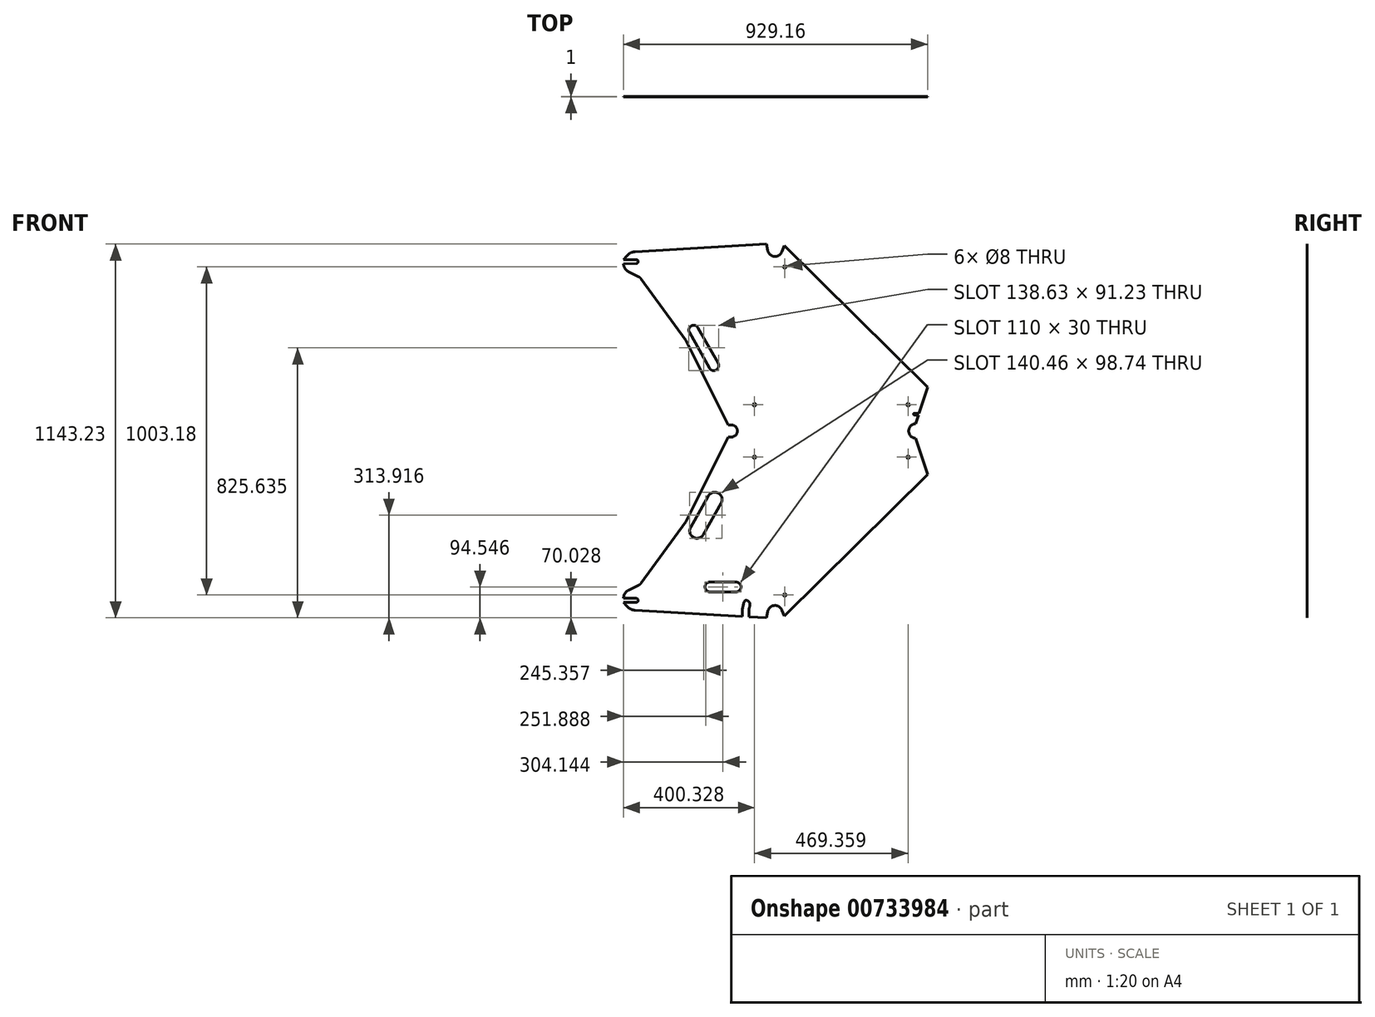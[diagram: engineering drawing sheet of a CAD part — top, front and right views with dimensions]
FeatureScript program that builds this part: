
annotation { "Feature Type Name" : "Feature", "Feature Type Description" : "" }
export const myFeature = defineFeature(function(context is Context, id is Id, definition is map)
    precondition{}
    {
        {
            var Q0;
            Q0=qCreatedBy(makeId("Front.planeOp"),FACE);
            var sketch = newSketch(context, id + "F0", { "sketchPlane" : qUnion([Q0])});
            skLineSegment(sketch, "E0", {"start": v(-160.76, 555.88) * mm, "end": v(408.24, 555.88) * mm, "construction": true});
            skLineSegment(sketch, "E1", {"start": v(408.24, 555.88) * mm, "end": v(445.83, 440.87) * mm, "construction": true});
            skArc(sketch, "E2", {"start": v(0.74, 26.27) * mm, "mid": v(-22.4, 40.64) * mm, "end": v(-42.43, 22.2) * mm});
            skLineSegment(sketch, "E3", {"start": v(-20.28, 18.24) * mm, "end": v(-144.86, 555.88) * mm, "construction": true});
            skLineSegment(sketch, "E4", {"start": v(-160.76, 555.88) * mm, "end": v(-39.05, 30.64) * mm, "construction": true});
            skLineSegment(sketch, "E5", {"start": v(-128.12, 555.88) * mm, "end": v(-7.89, 37.02) * mm, "construction": true});
            skLineSegment(sketch, "E6", {"start": v(0, 0) * mm, "end": v(-484.19, 28.1) * mm, "construction": true});
            skLineSegment(sketch, "E7", {"start": v(-160.76, 555.88) * mm, "end": v(-484.19, 28.1) * mm, "construction": true});
            skLineSegment(sketch, "E8", {"start": v(445.83, 440.87) * mm, "end": v(0, 0) * mm, "construction": true});
            skPoint(sketch, "E9", {"position": v(-176.43, 530.3) * mm});
            skPoint(sketch, "E10", {"position": v(-312.28, 308.61) * mm});
            skLineSegment(sketch, "E11", {"start": v(-312.28, 308.61) * mm, "end": v(-292.67, 296.6) * mm, "construction": true});
            skLineSegment(sketch, "E12", {"start": v(-176.43, 530.3) * mm, "end": v(-292.67, 296.6) * mm});
            skLineSegment(sketch, "E13", {"start": v(-429.8, 108.64) * mm, "end": v(-292.67, 296.6) * mm});
            skLineSegment(sketch, "E14", {"start": v(397.8, 555.88) * mm, "end": v(-163.71, 555.88) * mm});
            skLineSegment(sketch, "E15", {"start": v(409.57, 551.8) * mm, "end": v(445.83, 440.87) * mm});
            skLineSegment(sketch, "E16", {"start": v(445.83, 440.87) * mm, "end": v(7.82, 7.73) * mm});
            skPoint(sketch, "E17", {"position": v(-45.92, 2.66) * mm});
            skPoint(sketch, "E18", {"position": v(7.82, 7.73) * mm});
            skArc(sketch, "E19", {"start": v(7.82, 7.73) * mm, "mid": v(-23.1, 48.1) * mm, "end": v(-45.92, 2.66) * mm, "construction": true});
            skLineSegment(sketch, "E20", {"start": v(-176.43, 530.3) * mm, "end": v(-163.71, 555.88) * mm});
            skLineSegment(sketch, "E21", {"start": v(-173.75, 373) * mm, "end": v(-249.95, 238.03) * mm, "construction": true});
            skLineSegment(sketch, "E22", {"start": v(-186.81, 380.38) * mm, "end": v(-263, 245.4) * mm, "construction": true});
            skPoint(sketch, "E23.visualSharp", {"position": v(-289.13, 260.15) * mm});
            skPoint(sketch, "E24.visualSharp", {"position": v(-249.95, 238.03) * mm});
            skLineSegment(sketch, "E25", {"start": v(-212.94, 395.13) * mm, "end": v(-289.13, 260.15) * mm, "construction": true});
            skLineSegment(sketch, "E26", {"start": v(-249.95, 238.03) * mm, "end": v(-289.13, 260.15) * mm, "construction": true});
            skLineSegment(sketch, "E27", {"start": v(-212.94, 395.13) * mm, "end": v(-173.75, 373) * mm, "construction": true});
            skLineSegment(sketch, "E28", {"start": v(-292.67, 296.6) * mm, "end": v(-274.39, 286.27) * mm, "construction": true});
            skArc(sketch, "E29", {"start": v(-278.07, 279.74) * mm, "mid": v(-269.54, 249.09) * mm, "end": v(-238.88, 257.62) * mm});
            skLineSegment(sketch, "E30", {"start": v(-278.07, 279.74) * mm, "end": v(-238.88, 257.62) * mm, "construction": true});
            skArc(sketch, "E31", {"start": v(-184.81, 353.41) * mm, "mid": v(-193.34, 384.07) * mm, "end": v(-224, 375.53) * mm});
            skLineSegment(sketch, "E32", {"start": v(-224, 375.53) * mm, "end": v(-184.81, 353.41) * mm, "construction": true});
            skLineSegment(sketch, "E33", {"start": v(-278.07, 279.74) * mm, "end": v(-224, 375.53) * mm});
            skLineSegment(sketch, "E34", {"start": v(-184.81, 353.41) * mm, "end": v(-238.88, 257.62) * mm});
            skLineSegment(sketch, "E35.bottom", {"start": v(-234.19, 112.2) * mm, "end": v(-124.19, 112.2) * mm, "construction": true});
            skLineSegment(sketch, "E35.top", {"start": v(-234.19, 82.2) * mm, "end": v(-124.19, 82.2) * mm, "construction": true});
            skLineSegment(sketch, "E35.left", {"start": v(-234.19, 112.2) * mm, "end": v(-234.19, 82.2) * mm, "construction": true});
            skLineSegment(sketch, "E35.right", {"start": v(-124.19, 112.2) * mm, "end": v(-124.19, 82.2) * mm, "construction": true});
            skLineSegment(sketch, "E36", {"start": v(-124.19, 82.2) * mm, "end": v(-124.19, 7.2) * mm, "construction": true});
            skArc(sketch, "E37", {"start": v(-219.19, 112.2) * mm, "mid": v(-234.19, 97.2) * mm, "end": v(-219.19, 82.2) * mm});
            skArc(sketch, "E38", {"start": v(-139.19, 82.2) * mm, "mid": v(-124.19, 97.2) * mm, "end": v(-139.19, 112.2) * mm});
            skLineSegment(sketch, "E39", {"start": v(-139.19, 112.2) * mm, "end": v(-139.19, 82.2) * mm, "construction": true});
            skLineSegment(sketch, "E40", {"start": v(-219.19, 112.2) * mm, "end": v(-139.19, 112.2) * mm});
            skLineSegment(sketch, "E41", {"start": v(-139.19, 82.2) * mm, "end": v(-219.19, 82.2) * mm});
            skLineSegment(sketch, "E42", {"start": v(-641.86, 574.28) * mm, "end": v(862.04, 574.28) * mm, "construction": true});
            skLineSegment(sketch, "E43.MirrorCS", {"start": v(-312.28, 839.94) * mm, "end": v(-292.67, 851.96) * mm, "construction": true});
            skLineSegment(sketch, "E44.MirrorCS", {"start": v(-176.43, 618.26) * mm, "end": v(-163.71, 592.68) * mm});
            skLineSegment(sketch, "E45.MirrorCS", {"start": v(-249.95, 910.53) * mm, "end": v(-289.13, 888.41) * mm, "construction": true});
            skLineSegment(sketch, "E46.MirrorCS", {"start": v(-447.54, 1122.59) * mm, "end": v(-461.2, 1082.95) * mm, "construction": true});
            skLineSegment(sketch, "E47.MirrorCS", {"start": v(-212.94, 753.43) * mm, "end": v(-173.75, 775.55) * mm, "construction": true});
            skLineSegment(sketch, "E48.MirrorCS", {"start": v(-292.67, 851.96) * mm, "end": v(-274.39, 862.29) * mm, "construction": true});
            skLineSegment(sketch, "E49.MirrorCS", {"start": v(-45.92, 1145.9) * mm, "end": v(-447.54, 1122.59) * mm});
            skArc(sketch, "E50.MirrorC", {"start": v(0.74, 1122.29) * mm, "mid": v(-22.4, 1107.92) * mm, "end": v(-42.43, 1126.36) * mm});
            skLineSegment(sketch, "E51.MirrorCS", {"start": v(445.83, 707.7) * mm, "end": v(7.82, 1140.82) * mm});
            skLineSegment(sketch, "E52.MirrorCS", {"start": v(397.8, 592.68) * mm, "end": v(-163.71, 592.68) * mm});
            skLineSegment(sketch, "E53.MirrorCS", {"start": v(409.57, 596.75) * mm, "end": v(418.05, 622.68) * mm});
            skArc(sketch, "E54.MirrorCS", {"start": v(7.82, 1140.82) * mm, "mid": v(-23.1, 1100.45) * mm, "end": v(-45.92, 1145.9) * mm, "construction": true});
            skPoint(sketch, "E55.MirrorP", {"position": v(-289.13, 888.41) * mm});
            skLineSegment(sketch, "E56.MirrorCS", {"start": v(-20.28, 1130.32) * mm, "end": v(-144.86, 592.68) * mm, "construction": true});
            skPoint(sketch, "E57.MirrorP", {"position": v(-312.28, 839.94) * mm});
            skLineSegment(sketch, "E58.MirrorCS", {"start": v(-128.12, 592.68) * mm, "end": v(-7.89, 1111.54) * mm, "construction": true});
            skPoint(sketch, "E59.MirrorP", {"position": v(-176.43, 618.26) * mm});
            skPoint(sketch, "E60.MirrorP", {"position": v(-45.92, 1145.9) * mm});
            skLineSegment(sketch, "E61.MirrorCS", {"start": v(-160.76, 592.68) * mm, "end": v(397.8, 592.68) * mm, "construction": true});
            skPoint(sketch, "E62.MirrorP", {"position": v(7.82, 1140.82) * mm});
            skLineSegment(sketch, "E63.MirrorCS", {"start": v(-160.76, 592.68) * mm, "end": v(-39.05, 1117.92) * mm, "construction": true});
            skLineSegment(sketch, "E64.MirrorCS", {"start": v(-160.76, 592.68) * mm, "end": v(-484.19, 1120.46) * mm, "construction": true});
            skLineSegment(sketch, "E65.MirrorCS", {"start": v(-186.81, 768.18) * mm, "end": v(-263, 903.16) * mm, "construction": true});
            skPoint(sketch, "E66.MirrorP", {"position": v(-249.95, 910.53) * mm});
            skPoint(sketch, "E67.MirrorP", {"position": v(-461.2, 1082.95) * mm});
            skLineSegment(sketch, "E68.MirrorCS", {"start": v(445.83, 707.7) * mm, "end": v(0, 1148.56) * mm, "construction": true});
            skLineSegment(sketch, "E69.MirrorCS", {"start": v(409.57, 596.75) * mm, "end": v(418.05, 622.68) * mm, "construction": true});
            skLineSegment(sketch, "E70.MirrorCS", {"start": v(-461.2, 1082.95) * mm, "end": v(-292.67, 851.96) * mm});
            skLineSegment(sketch, "E71.MirrorCS", {"start": v(-176.43, 618.26) * mm, "end": v(-178.63, 622.68) * mm});
            skLineSegment(sketch, "E72.MirrorCS", {"start": v(0, 1148.56) * mm, "end": v(-484.19, 1120.46) * mm, "construction": true});
            skLineSegment(sketch, "E73", {"start": v(-255.63, 890.1) * mm, "end": v(-194.19, 781.24) * mm});
            skArc(sketch, "E74", {"start": v(-255.63, 890.1) * mm, "mid": v(-276.07, 895.78) * mm, "end": v(-281.76, 875.35) * mm});
            skLineSegment(sketch, "E75", {"start": v(-289.13, 888.41) * mm, "end": v(-212.94, 753.43) * mm, "construction": true});
            skLineSegment(sketch, "E76", {"start": v(-281.76, 875.35) * mm, "end": v(-255.63, 890.1) * mm, "construction": true});
            skArc(sketch, "E77", {"start": v(-220.31, 766.5) * mm, "mid": v(-199.88, 760.8) * mm, "end": v(-194.19, 781.24) * mm});
            skLineSegment(sketch, "E78", {"start": v(-220.31, 766.5) * mm, "end": v(-194.19, 781.24) * mm, "construction": true});
            skLineSegment(sketch, "E79", {"start": v(-281.76, 875.35) * mm, "end": v(-220.31, 766.5) * mm});
            skArc(sketch, "E80.trimOffspring", {"start": v(-153.71, 555.88) * mm, "mid": v(-135.31, 574.28) * mm, "end": v(-153.71, 592.68) * mm});
            skArc(sketch, "E81", {"start": v(409.57, 596.75) * mm, "mid": v(388.24, 574.28) * mm, "end": v(409.57, 551.8) * mm});
            skLineSegment(sketch, "E82", {"start": v(388.24, 592.68) * mm, "end": v(388.24, 555.88) * mm, "construction": true});
            skPoint(sketch, "E83.orphan", {"position": v(408.24, 592.68) * mm});
            skPoint(sketch, "E84.orphan", {"position": v(408.24, 555.88) * mm});
            skLineSegment(sketch, "E85", {"start": v(-437.04, 102.52) * mm, "end": v(-516.22, 63.05) * mm, "construction": true});
            skLineSegment(sketch, "E86", {"start": v(-516.22, 63.05) * mm, "end": v(-444.22, 62.36) * mm, "construction": true});
            skLineSegment(sketch, "E87", {"start": v(-438.28, 56.3) * mm, "end": v(-438.28, 56.3) * mm});
            skLineSegment(sketch, "E88", {"start": v(-444.33, 50.36) * mm, "end": v(-483.33, 50.74) * mm});
            skLineSegment(sketch, "E89", {"start": v(-483.33, 50.74) * mm, "end": v(-463.52, 26.9) * mm});
            skPoint(sketch, "E90.orphan", {"position": v(-439.25, 101.42) * mm});
            skPoint(sketch, "E91.end.orphan", {"position": v(-461.2, 65.61) * mm});
            skArc(sketch, "E92", {"start": v(-467.98, 87.1) * mm, "mid": v(-479.03, 77.06) * mm, "end": v(-483.22, 62.74) * mm});
            skLineSegment(sketch, "E93", {"start": v(-483.22, 62.74) * mm, "end": v(-482.71, 115.9) * mm, "construction": true});
            skPoint(sketch, "E94.visualSharp", {"position": v(-438.22, 62.3) * mm});
            skArc(sketch, "E94.filletArc", {"start": v(-438.28, 56.3) * mm, "mid": v(-440, 60.57) * mm, "end": v(-444.22, 62.36) * mm});
            skPoint(sketch, "E95.visualSharp", {"position": v(-438.33, 50.3) * mm});
            skArc(sketch, "E95.filletArc", {"start": v(-444.33, 50.36) * mm, "mid": v(-440.07, 52.08) * mm, "end": v(-438.28, 56.3) * mm});
            skLineSegment(sketch, "E96", {"start": v(-467.98, 87.1) * mm, "end": v(-437.04, 102.52) * mm, "construction": true});
            skLineSegment(sketch, "E97", {"start": v(-467.98, 87.1) * mm, "end": v(-437.04, 102.52) * mm});
            skLineSegment(sketch, "E98", {"start": v(-483.22, 62.74) * mm, "end": v(-444.22, 62.36) * mm});
            skLineSegment(sketch, "E99", {"start": v(-463.52, 26.9) * mm, "end": v(-447.54, 25.97) * mm, "construction": true});
            skArc(sketch, "E100", {"start": v(-473.74, 39.2) * mm, "mid": v(-462.02, 29.86) * mm, "end": v(-447.54, 25.97) * mm});
            skLineSegment(sketch, "E101", {"start": v(-483.22, 62.74) * mm, "end": v(-483.33, 50.74) * mm, "construction": true});
            skPoint(sketch, "E102.visualSharp", {"position": v(-432.68, 104.7) * mm});
            skArc(sketch, "E102.filletArc", {"start": v(-437.04, 102.52) * mm, "mid": v(-433.06, 105.15) * mm, "end": v(-429.8, 108.64) * mm});
            skLineSegment(sketch, "E103.MirrorCS", {"start": v(-467.98, 1061.46) * mm, "end": v(-437.04, 1046.03) * mm});
            skLineSegment(sketch, "E104.MirrorCS", {"start": v(-483.22, 1085.82) * mm, "end": v(-444.22, 1086.2) * mm});
            skArc(sketch, "E105.MirrorCS", {"start": v(-444.33, 1098.2) * mm, "mid": v(-440.07, 1096.48) * mm, "end": v(-438.28, 1092.25) * mm});
            skArc(sketch, "E106.MirrorCS", {"start": v(-438.28, 1092.25) * mm, "mid": v(-440, 1088) * mm, "end": v(-444.22, 1086.2) * mm});
            skArc(sketch, "E107.MirrorCS", {"start": v(-437.04, 1046.03) * mm, "mid": v(-433.06, 1043.41) * mm, "end": v(-429.8, 1039.92) * mm});
            skLineSegment(sketch, "E108.MirrorCS", {"start": v(-444.33, 1098.2) * mm, "end": v(-483.33, 1097.82) * mm});
            skLineSegment(sketch, "E109.MirrorCS", {"start": v(-463.52, 1121.66) * mm, "end": v(-447.54, 1122.59) * mm, "construction": true});
            skPoint(sketch, "E110.MirrorP", {"position": v(-438.22, 1086.25) * mm});
            skArc(sketch, "E111.MirrorCS", {"start": v(-473.74, 1109.36) * mm, "mid": v(-462.02, 1118.7) * mm, "end": v(-447.54, 1122.59) * mm});
            skLineSegment(sketch, "E112.MirrorCS", {"start": v(-516.22, 1085.5) * mm, "end": v(-444.22, 1086.2) * mm, "construction": true});
            skLineSegment(sketch, "E113.MirrorCS", {"start": v(-483.22, 1085.82) * mm, "end": v(-482.71, 1032.66) * mm, "construction": true});
            skArc(sketch, "E114.MirrorCS", {"start": v(-467.98, 1061.46) * mm, "mid": v(-479.03, 1071.5) * mm, "end": v(-483.22, 1085.82) * mm});
            skLineSegment(sketch, "E115.MirrorCS", {"start": v(-483.33, 1097.82) * mm, "end": v(-463.52, 1121.66) * mm});
            skPoint(sketch, "E116.MirrorP", {"position": v(-432.68, 1043.86) * mm});
            skPoint(sketch, "E117.MirrorP", {"position": v(-438.33, 1098.25) * mm});
            skLineSegment(sketch, "E118.MirrorCS", {"start": v(-467.98, 1061.46) * mm, "end": v(-437.04, 1046.03) * mm, "construction": true});
            skLineSegment(sketch, "E119.MirrorCS", {"start": v(-437.04, 1046.03) * mm, "end": v(-516.22, 1085.5) * mm, "construction": true});
            skLineSegment(sketch, "E120.MirrorCS", {"start": v(-483.22, 1085.82) * mm, "end": v(-483.33, 1097.82) * mm, "construction": true});
            skPoint(sketch, "E121.MirrorP", {"position": v(-439.25, 1047.14) * mm});
            skLineSegment(sketch, "E122", {"start": v(-91.14, 55.37) * mm, "end": v(-109, 56.4) * mm});
            skCircle(sketch, "E123", {"center": v(-20.28, 18.24) * mm, "radius": 100 * mm, "construction": true});
            skCircle(sketch, "E124", {"center": v(-20.28, 18.24) * mm, "radius": 80 * mm, "construction": true});
            skArc(sketch, "E125", {"start": v(-113.98, 53.16) * mm, "mid": v(-119.54, 30.39) * mm, "end": v(-119.64, 6.94) * mm});
            skArc(sketch, "E126", {"start": v(-91.14, 55.37) * mm, "mid": v(-99.22, 31.23) * mm, "end": v(-99.3, 5.76) * mm});
            skPoint(sketch, "E127.visualSharp", {"position": v(-112.62, 56.62) * mm});
            skArc(sketch, "E127.filletArc", {"start": v(-109, 56.4) * mm, "mid": v(-112.03, 55.6) * mm, "end": v(-113.98, 53.16) * mm});
            skLineSegment(sketch, "E128", {"start": v(-119.64, 6.94) * mm, "end": v(-447.54, 25.97) * mm});
            skLineSegment(sketch, "E129", {"start": v(-99.3, 5.76) * mm, "end": v(-45.92, 2.66) * mm});
            skCircle(sketch, "E130", {"center": v(-83, 654.48) * mm, "radius": 4 * mm});
            skCircle(sketch, "E131", {"center": v(386.36, 654.48) * mm, "radius": 4 * mm});
            skCircle(sketch, "E132", {"center": v(9.5, 1075.87) * mm, "radius": 4 * mm});
            skLineSegment(sketch, "E133", {"start": v(-120.75, 624.48) * mm, "end": v(418.63, 624.48) * mm, "construction": true});
            skLineSegment(sketch, "E134", {"start": v(437.88, 715.55) * mm, "end": v(397.7, 592.61) * mm, "construction": true});
            skLineSegment(sketch, "E135", {"start": v(0, 1108.22) * mm, "end": v(435.87, 677.2) * mm, "construction": true});
            skCircle(sketch, "E136.MirrorC", {"center": v(9.5, 72.69) * mm, "radius": 4 * mm});
            skCircle(sketch, "E137.MirrorC", {"center": v(-83, 494.08) * mm, "radius": 4 * mm});
            skCircle(sketch, "E138.MirrorC", {"center": v(386.36, 494.08) * mm, "radius": 4 * mm});
            skLineSegment(sketch, "E139", {"start": v(-153.71, 592.68) * mm, "end": v(-153.71, 555.88) * mm, "construction": true});
            skLineSegment(sketch, "E140", {"start": v(-42.43, 22.2) * mm, "end": v(-45.92, 2.66) * mm});
            skLineSegment(sketch, "E141", {"start": v(0.74, 26.27) * mm, "end": v(7.82, 7.73) * mm});
            skLineSegment(sketch, "E142", {"start": v(-45.92, 1145.9) * mm, "end": v(-42.43, 1126.36) * mm});
            skLineSegment(sketch, "E143", {"start": v(0.74, 1122.29) * mm, "end": v(7.82, 1140.82) * mm});
            skArc(sketch, "E144", {"start": v(-97.28, 39.95) * mm, "mid": v(-99.2, 50.99) * mm, "end": v(-109, 56.4) * mm});
            skLineSegment(sketch, "E145", {"start": v(-530.7, 62.82) * mm, "end": v(-438.1, 61.94) * mm, "construction": true});
            skLineSegment(sketch, "E146", {"start": v(-438.1, 61.94) * mm, "end": v(-438.2, 50.97) * mm, "construction": true});
            skLineSegment(sketch, "E147", {"start": v(-438.2, 50.97) * mm, "end": v(-529.63, 51.84) * mm, "construction": true});
            skLineSegment(sketch, "E148.trimOffspring", {"start": v(-178.63, 622.68) * mm, "end": v(-292.67, 851.96) * mm});
            skLineSegment(sketch, "E149", {"start": v(431.28, 622.68) * mm, "end": v(406.05, 622.68) * mm, "construction": true});
            skLineSegment(sketch, "E150", {"start": v(418.05, 622.68) * mm, "end": v(403.05, 622.68) * mm});
            skLineSegment(sketch, "E151", {"start": v(403.05, 625.68) * mm, "end": v(403.05, 625.68) * mm});
            skLineSegment(sketch, "E152", {"start": v(406.05, 628.68) * mm, "end": v(420, 628.68) * mm});
            skPoint(sketch, "E153.visualSharp", {"position": v(403.05, 628.68) * mm});
            skArc(sketch, "E153.filletArc", {"start": v(406.05, 628.68) * mm, "mid": v(403.92, 627.8) * mm, "end": v(403.05, 625.68) * mm});
            skPoint(sketch, "E154.newPointA", {"position": v(403.05, 622.68) * mm});
            skArc(sketch, "E154.filletArc", {"start": v(403.05, 625.68) * mm, "mid": v(403.92, 623.56) * mm, "end": v(406.05, 622.68) * mm});
            skLineSegment(sketch, "E155.trimOffspring", {"start": v(420, 628.68) * mm, "end": v(445.83, 707.7) * mm, "construction": true});
            skLineSegment(sketch, "E156.trimOffspring", {"start": v(420, 628.68) * mm, "end": v(445.83, 707.7) * mm});
            skSolve(sketch);
        }
        {
            var Q0;
            Q0=qSketchRegion(id+"F0",true);
            extrude(context, id + "F1", {"entities" : qUnion([Q0]), "depth" : 1 * mm, "offsetDistance" : 25 * mm});
        }
    });
